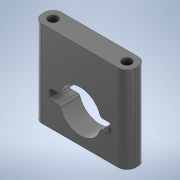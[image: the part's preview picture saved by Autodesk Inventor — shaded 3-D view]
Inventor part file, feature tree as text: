
AUTODESK INVENTOR PART (.ipt)
format: ipt  version: 2020 (Build 240168000, 168)  size: 188,416 bytes
history: native  units: mm
features: projected_geometry x7, sketch x4, extrude x3, fillet x2, other x1
ambient origin geometry x8: Origin, YZ Plane, XZ Plane, XY Plane, X Axis, Y Axis, Z Axis, Center Point
bodies: Body1 (feature_tree)
feature tree (17):
  other  "Твердое тело1"
  sketch  "Эскиз1"
  extrude  "Выдавливание1"  Depth=30.0mm
  fillet  "Сопряжение1"  Radius=3.8mm
  extrude  "Выдавливание2"  Depth=38.0mm
  extrude  "Выдавливание3"  Depth=8.0mm
  fillet  "Сопряжение2"  Radius=35.0mm
  sketch  "Эскиз2"
  sketch  "Эскиз3"
  projected_geometry  "Спроецированная петля1"
  projected_geometry  "Спроецированная петля2"
  projected_geometry  "Спроецированная петля3"
  projected_geometry  "Спроецированная петля4"
  projected_geometry  "Спроецированная петля5"
  projected_geometry  "Спроецированная петля6"
  sketch  "Эскиз4"
  projected_geometry  "Спроецированная петля7"
